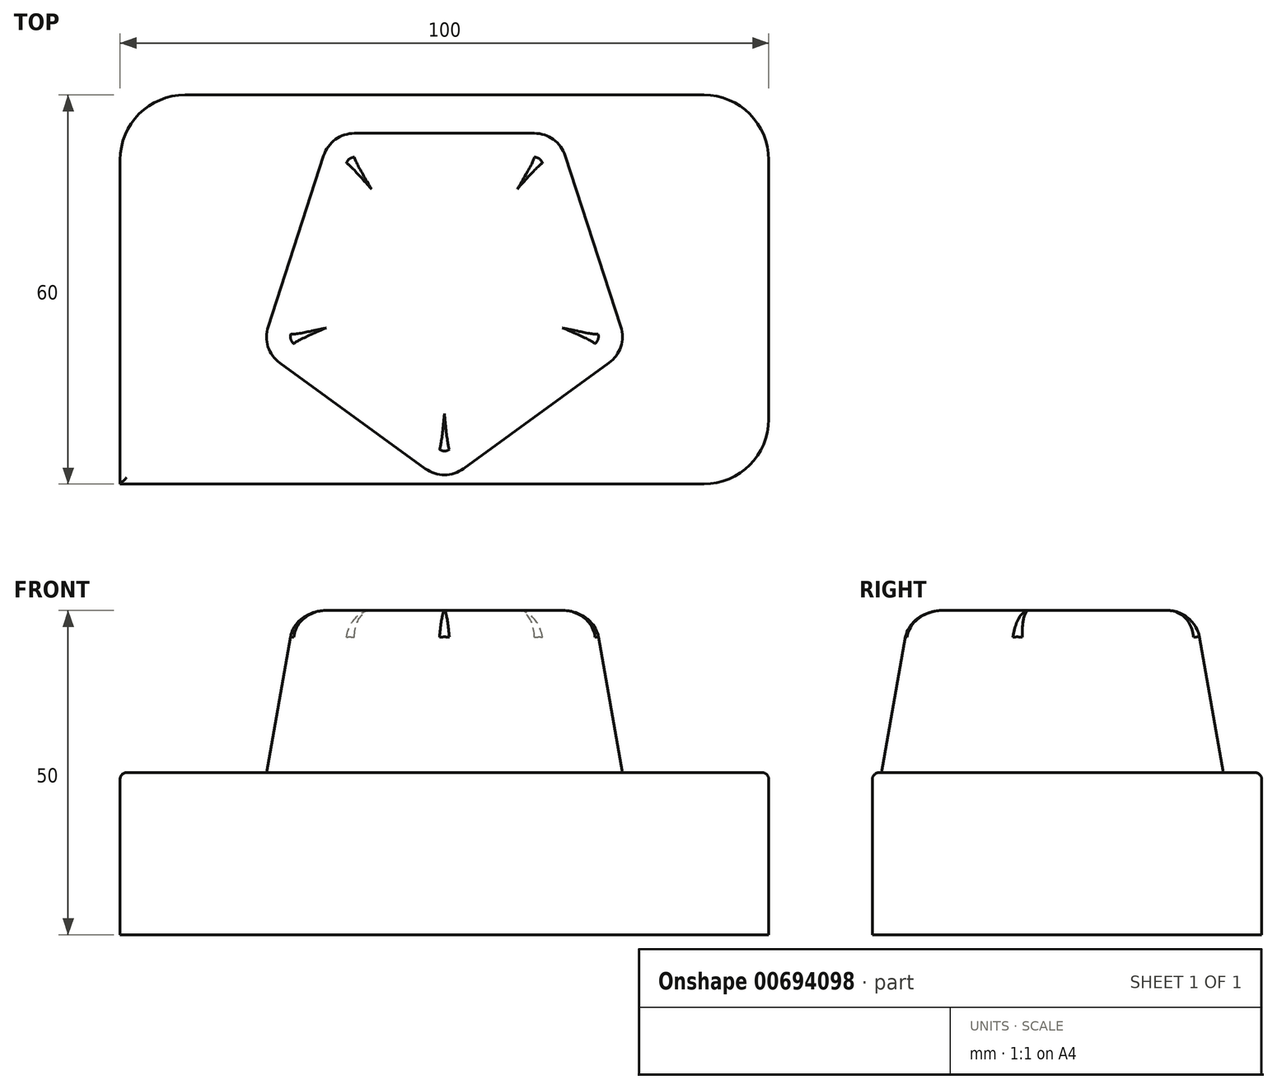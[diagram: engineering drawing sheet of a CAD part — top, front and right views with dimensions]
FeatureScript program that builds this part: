
annotation { "Feature Type Name" : "Feature", "Feature Type Description" : "" }
export const myFeature = defineFeature(function(context is Context, id is Id, definition is map)
    precondition{}
    {
        {
            var Q0;
            Q0=qCreatedBy(makeId("Top.planeOp"),FACE);
            var sketch = newSketch(context, id + "F0", { "sketchPlane" : qUnion([Q0])});
            skLineSegment(sketch, "E0.bottom", {"start": v(-40, 30) * mm, "end": v(40, 30) * mm});
            skLineSegment(sketch, "E0.top", {"start": v(-50, -30) * mm, "end": v(40, -30) * mm});
            skLineSegment(sketch, "E0.left", {"start": v(-50, 20) * mm, "end": v(-50, -30) * mm});
            skLineSegment(sketch, "E0.right", {"start": v(50, 20) * mm, "end": v(50, -20) * mm});
            skCircle(sketch, "E1", {"center": v(91.89, 50.48) * mm, "radius": 10.23 * mm});
            skLineSegment(sketch, "E2", {"start": v(0, 30) * mm, "end": v(0, -30) * mm, "construction": true});
            skLineSegment(sketch, "E3", {"start": v(-50, 0) * mm, "end": v(50, 0) * mm, "construction": true});
            skPoint(sketch, "E4.visualSharp", {"position": v(-50, 30) * mm});
            skArc(sketch, "E4.filletArc", {"start": v(-40, 30) * mm, "mid": v(-47.07, 27.07) * mm, "end": v(-50, 20) * mm});
            skPoint(sketch, "E5.visualSharp", {"position": v(50, 30) * mm});
            skArc(sketch, "E5.filletArc", {"start": v(50, 20) * mm, "mid": v(47.07, 27.07) * mm, "end": v(40, 30) * mm});
            skPoint(sketch, "E6.visualSharp", {"position": v(50, -30) * mm});
            skArc(sketch, "E6.filletArc", {"start": v(40, -30) * mm, "mid": v(47.07, -27.07) * mm, "end": v(50, -20) * mm});
            skSolve(sketch);
        }
        {
            var Q0;
            Q0=makeQuery(id+"F0.imprint","IMPRINT",FACE,{"disambiguationData":[TD([[makeQuery(id+"F0.imprint","IMPRINT",EDGE,{"derivedFrom":sQuery(id+"F0.wireOp",EDGE,"E0.bottom")}),-1.0]])]});
            extrude(context, id + "F1", {"entities" : qUnion([Q0]), "depth" : 25 * mm, "offsetDistance" : 25 * mm});
        }
        {
            var Q0;
            Q0=makeQuery(id+"F1.opExtrude","CAP_FACE",FACE,{"disambiguationData":[OSD([sQuery(id+"F0.wireOp",EDGE,"E0.bottom"),sQuery(id+"F0.wireOp",EDGE,"E0.top"),sQuery(id+"F0.wireOp",EDGE,"E0.left"),sQuery(id+"F0.wireOp",EDGE,"E0.right"),sQuery(id+"F0.wireOp",EDGE,"E4.filletArc"),sQuery(id+"F0.wireOp",EDGE,"E5.filletArc"),sQuery(id+"F0.wireOp",EDGE,"E6.filletArc")])],"isStart":false});
            var sketch = newSketch(context, id + "F2", { "sketchPlane" : qUnion([Q0])});
            skCircle(sketch, "E7.cCircle", {"center": v(0, 0) * mm, "radius": 24.09 * mm, "construction": true});
            skLineSegment(sketch, "E7.0", {"start": v(-13.87, 24.09) * mm, "end": v(13.87, 24.09) * mm});
            skLineSegment(sketch, "E7.1", {"start": v(18.62, 20.63) * mm, "end": v(27.2, -5.75) * mm});
            skLineSegment(sketch, "E7.2", {"start": v(25.38, -11.34) * mm, "end": v(2.94, -27.64) * mm});
            skLineSegment(sketch, "E7.3", {"start": v(-2.94, -27.64) * mm, "end": v(-25.38, -11.34) * mm});
            skLineSegment(sketch, "E7.4", {"start": v(-27.2, -5.75) * mm, "end": v(-18.62, 20.63) * mm});
            skPoint(sketch, "E7.0.midPoint", {"position": v(0, 24.09) * mm});
            skPoint(sketch, "E8.visualSharp", {"position": v(-17.5, 24.09) * mm});
            skArc(sketch, "E8.filletArc", {"start": v(-13.87, 24.09) * mm, "mid": v(-16.8, 23.13) * mm, "end": v(-18.62, 20.63) * mm});
            skPoint(sketch, "E9.visualSharp", {"position": v(-28.32, -9.2) * mm});
            skArc(sketch, "E9.filletArc", {"start": v(-27.2, -5.75) * mm, "mid": v(-27.2, -8.84) * mm, "end": v(-25.38, -11.34) * mm});
            skPoint(sketch, "E10.visualSharp", {"position": v(0, -29.77) * mm});
            skArc(sketch, "E10.filletArc", {"start": v(-2.94, -27.64) * mm, "mid": v(0, -28.6) * mm, "end": v(2.94, -27.64) * mm});
            skPoint(sketch, "E11.visualSharp", {"position": v(17.5, 24.09) * mm});
            skArc(sketch, "E11.filletArc", {"start": v(18.62, 20.63) * mm, "mid": v(16.8, 23.13) * mm, "end": v(13.87, 24.09) * mm});
            skPoint(sketch, "E12.visualSharp", {"position": v(28.32, -9.2) * mm});
            skArc(sketch, "E12.filletArc", {"start": v(25.38, -11.34) * mm, "mid": v(27.2, -8.84) * mm, "end": v(27.2, -5.75) * mm});
            skSolve(sketch);
        }
        {
            var Q0;
            Q0=makeQuery(id+"F2.imprint","IMPRINT",FACE,{"disambiguationData":[TD([[makeQuery(id+"F2.imprint","IMPRINT",EDGE,{"derivedFrom":sQuery(id+"F2.wireOp",EDGE,"E7.0")}),-1.0]])]});
            extrude(context, id + "F3", {"entities" : qUnion([Q0]), "operationType" : NewBodyOperationType.ADD, "depth" : 25 * mm, "offsetDistance" : 25 * mm, "hasDraft" : true, "draftAngle" : 10 * degree, "draftPullDirection" : true});
        }
        {
            var Q0;
            Q0=makeQuery(id+"F1.opExtrude","CAP_EDGE",EDGE,{"disambiguationData":[OSD([sQuery(id+"F0.wireOp",EDGE,"E0.top")])],"isStart":false});
            fillet(context, id + "F4", {"entities" : qUnion([Q0]), "radius" : 1 * mm, "tangentPropagation" : true, "allowEdgeOverflow" : false});
        }
        {
            var Q0;
            Q0=makeQuery(id+"F3.opExtrude","CAP_FACE",FACE,{"disambiguationData":[OSD([sQuery(id+"F2.wireOp",EDGE,"E7.0"),sQuery(id+"F2.wireOp",EDGE,"E7.1"),sQuery(id+"F2.wireOp",EDGE,"E7.2"),sQuery(id+"F2.wireOp",EDGE,"E7.3"),sQuery(id+"F2.wireOp",EDGE,"E7.4"),sQuery(id+"F2.wireOp",EDGE,"E8.filletArc"),sQuery(id+"F2.wireOp",EDGE,"E9.filletArc"),sQuery(id+"F2.wireOp",EDGE,"E10.filletArc"),sQuery(id+"F2.wireOp",EDGE,"E11.filletArc"),sQuery(id+"F2.wireOp",EDGE,"E12.filletArc")])],"isStart":false});
            fillet(context, id + "F5", {"entities" : qUnion([Q0]), "radius" : 5 * mm, "tangentPropagation" : true, "allowEdgeOverflow" : false});
        }
    });
